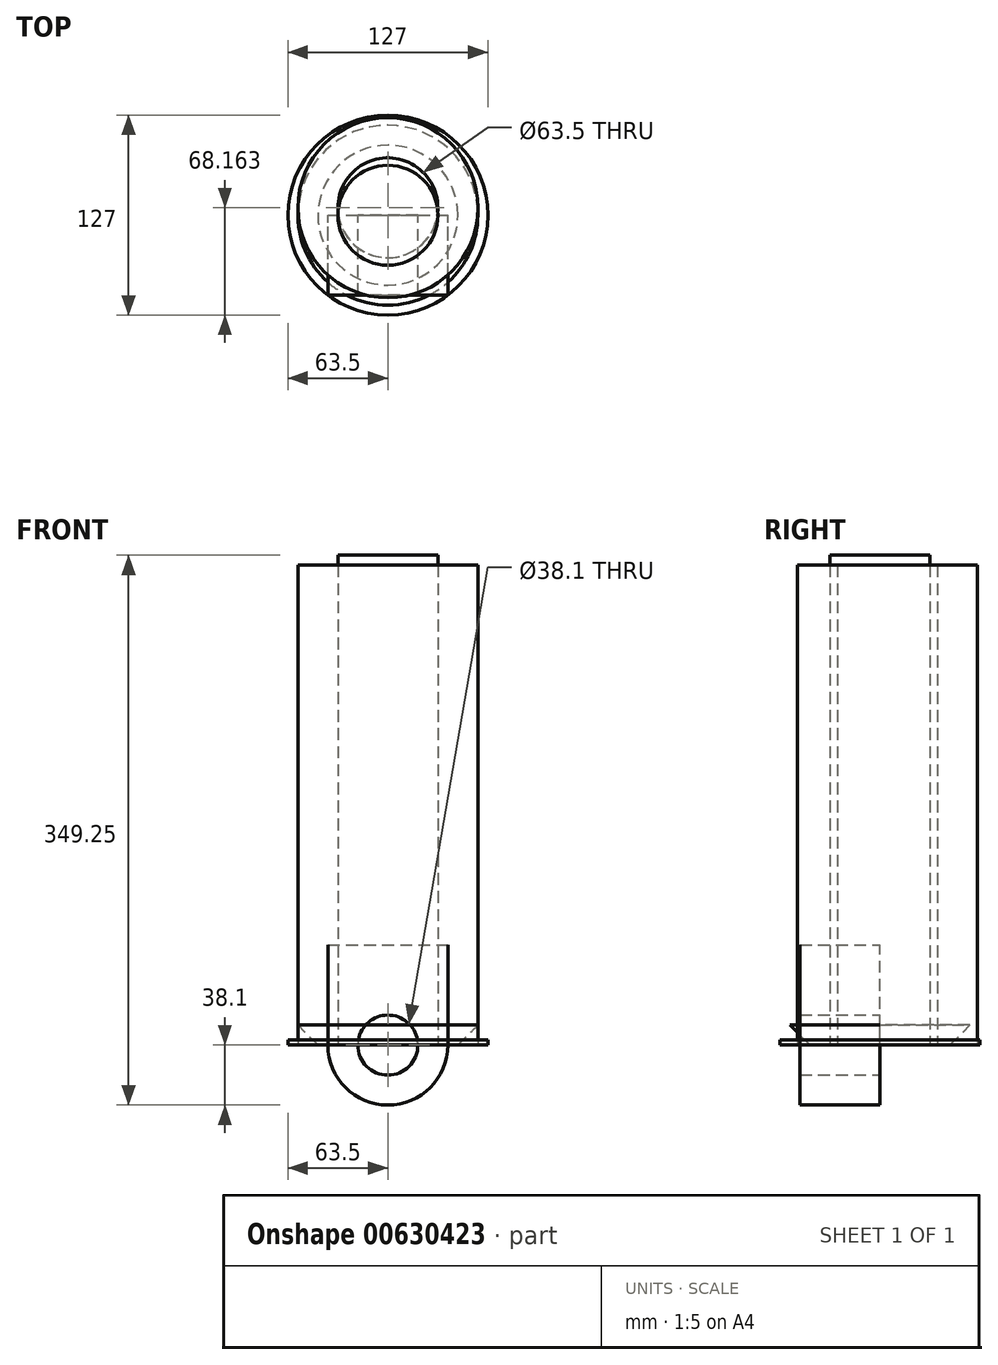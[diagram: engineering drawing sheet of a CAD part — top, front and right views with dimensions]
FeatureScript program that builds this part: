
annotation { "Feature Type Name" : "Feature", "Feature Type Description" : "" }
export const myFeature = defineFeature(function(context is Context, id is Id, definition is map)
    precondition{}
    {
        {
            var Q0;
            Q0=qCreatedBy(makeId("Front.planeOp"),FACE);
            var sketch = newSketch(context, id + "F0", { "sketchPlane" : qUnion([Q0])});
            skCircle(sketch, "E0", {"center": v(0, 0) * mm, "radius": 38.1 * mm});
            skCircle(sketch, "E1", {"center": v(0, 0) * mm, "radius": 19.05 * mm});
            skLineSegment(sketch, "E2", {"start": v(38.1, 0) * mm, "end": v(38.1, 63.5) * mm});
            skLineSegment(sketch, "E3", {"start": v(-38.1, 0) * mm, "end": v(-38.1, 63.5) * mm});
            skLineSegment(sketch, "E4", {"start": v(-38.1, 63.5) * mm, "end": v(38.1, 63.5) * mm});
            skSolve(sketch);
        }
        {
            var Q0;
            Q0 = qSketchRegion(id + "F0", true);
            extrude(context, id + "F1", {"entities" : qUnion([Q0]), "depth" : 50.8 * mm, "offsetDistance" : 25.4 * mm});
        }
        {
            var Q0;
            Q0=qCreatedBy(makeId("Top.planeOp"),FACE);
            var sketch = newSketch(context, id + "F2", { "sketchPlane" : qUnion([Q0])});
            skCircle(sketch, "E5", {"center": v(0, 0) * mm, "radius": 57.15 * mm});
            skSolve(sketch);
        }
        {
            var Q0;
            Q0 = qSketchRegion(id + "F2", true);
            extrude(context, id + "F3", {"entities" : qUnion([Q0]), "depth" : 12.7 * mm, "offsetDistance" : 25.4 * mm});
        }
        {
            var Q0;
            Q0=makeQuery(id+"F3.opExtrude","CAP_EDGE",EDGE,{"disambiguationData":[OSD([sQuery(id+"F2.wireOp",EDGE,"E5")])],"isStart":true});
            chamfer(context, id + "F4", {"entities" : qUnion([Q0]), "width" : 12.7 * mm, "tangentPropagation" : true});
        }
        {
            var Q0;
            Q0=qCreatedBy(makeId("Top.planeOp"),FACE);
            var sketch = newSketch(context, id + "F5", { "sketchPlane" : qUnion([Q0])});
            skCircle(sketch, "E6", {"center": v(0, 0) * mm, "radius": 63.5 * mm});
            skSolve(sketch);
        }
        {
            var Q0;
            Q0 = qSketchRegion(id + "F5", true);
            extrude(context, id + "F6", {"entities" : qUnion([Q0]), "depth" : 3.17 * mm, "offsetDistance" : 25.4 * mm});
        }
        {
            var Q0;
            Q0=qCreatedBy(makeId("Top.planeOp"),FACE);
            var sketch = newSketch(context, id + "F7", { "sketchPlane" : qUnion([Q0])});
            skCircle(sketch, "E7", {"center": v(0, 4.66) * mm, "radius": 57.15 * mm});
            skCircle(sketch, "E8", {"center": v(0, 4.66) * mm, "radius": 31.75 * mm});
            skSolve(sketch);
        }
        {
            var Q0;
            Q0 = qSketchRegion(id + "F7", true);
            extrude(context, id + "F8", {"entities" : qUnion([Q0]), "depth" : 304.8 * mm, "offsetDistance" : 25.4 * mm});
        }
        {
            var Q0;
            Q0=qCreatedBy(makeId("Top.planeOp"),FACE);
            var sketch = newSketch(context, id + "F9", { "sketchPlane" : qUnion([Q0])});
            skCircle(sketch, "E9", {"center": v(0, 0) * mm, "radius": 31.75 * mm});
            skSolve(sketch);
        }
        {
            var Q0;
            Q0 = qSketchRegion(id + "F9", true);
            extrude(context, id + "F10", {"entities" : qUnion([Q0]), "depth" : 311.15 * mm, "offsetDistance" : 25.4 * mm});
        }
        {
            var Q0;
            Q0=qCreatedBy(makeId("Front.planeOp"),FACE);
            var sketch = newSketch(context, id + "F11", { "sketchPlane" : qUnion([Q0])});
            skArc(sketch, "E10", {"start": v(0, 31.75) * mm, "mid": v(-31, -6.87) * mm, "end": v(13.42, -28.78) * mm});
            skCircle(sketch, "E11", {"center": v(0, 0) * mm, "radius": 19.05 * mm});
            skLineSegment(sketch, "E12", {"start": v(13.42, -28.78) * mm, "end": v(234.95, 0) * mm});
            skLineSegment(sketch, "E13", {"start": v(0, 0) * mm, "end": v(0, 31.75) * mm});
            skLineSegment(sketch, "E14", {"start": v(0, 31.75) * mm, "end": v(171.19, 141.23) * mm});
            skLineSegment(sketch, "E15", {"start": v(234.95, 0) * mm, "end": v(171.19, 141.23) * mm});
            skSolve(sketch);
        }
        {
            var Q0;
            Q0 = qSketchRegion(id + "F11", true);
            extrude(context, id + "F12", {"entities" : qUnion([Q0]), "depth" : 12.7 * mm, "offsetDistance" : 25.4 * mm});
        }
        {
            var Q0;
            Q0=makeQuery(id+"F12.opExtrude","SWEPT_BODY",BODY,{"disambiguationData":[OSD([sQuery(id+"F11.wireOp",EDGE,"E10"),sQuery(id+"F11.wireOp",EDGE,"E11"),sQuery(id+"F11.wireOp",EDGE,"E12"),sQuery(id+"F11.wireOp",EDGE,"E14"),sQuery(id+"F11.wireOp",EDGE,"E15")])]});
            deleteBodies(context, id + "F13", {"entities" : qUnion([Q0])});
        }
    });
